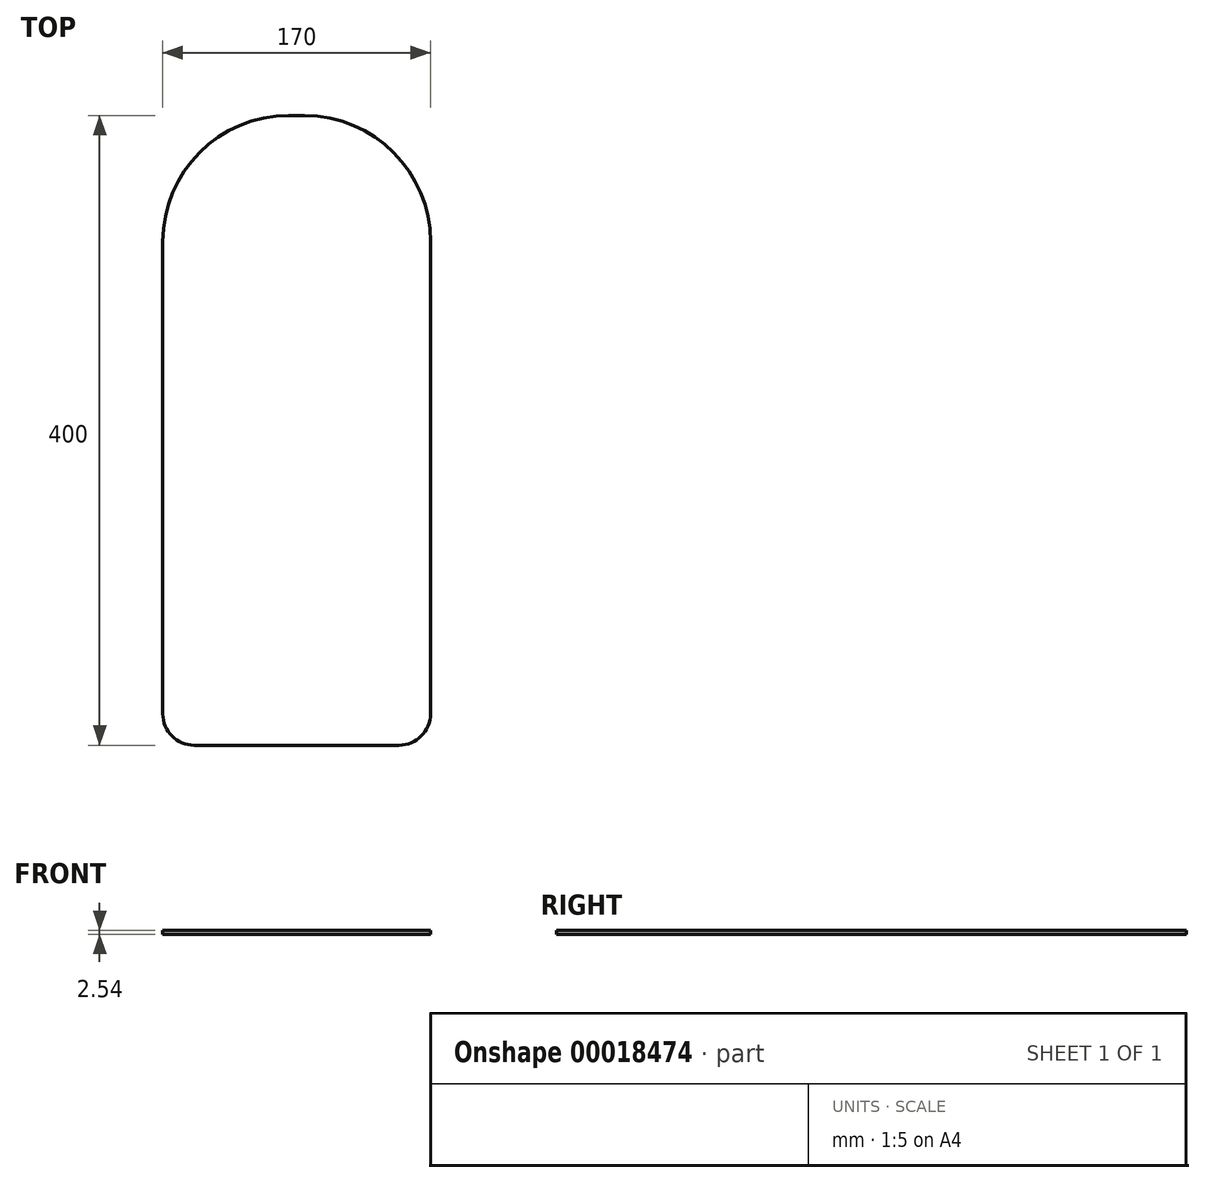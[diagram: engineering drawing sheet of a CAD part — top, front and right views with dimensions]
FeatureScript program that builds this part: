
annotation { "Feature Type Name" : "Feature", "Feature Type Description" : "" }
export const myFeature = defineFeature(function(context is Context, id is Id, definition is map)
    precondition{}
    {
        {
            var Q0;
            Q0=qCreatedBy(makeId("Top.planeOp"),FACE);
            var sketch = newSketch(context, id + "F0", { "sketchPlane" : qUnion([Q0])});
            skLineSegment(sketch, "E0.rect.bottom", {"start": v(65, -200) * mm, "end": v(-65, -200) * mm});
            skLineSegment(sketch, "E0.rect.top", {"start": v(5, 200) * mm, "end": v(-5, 200) * mm});
            skLineSegment(sketch, "E0.rect.left", {"start": v(85, -180) * mm, "end": v(85, 120) * mm});
            skLineSegment(sketch, "E0.rect.right", {"start": v(-85, -180) * mm, "end": v(-85, 120) * mm});
            skPoint(sketch, "E0.rect.middle", {"position": v(0, 0) * mm});
            skPoint(sketch, "E1.visualSharp", {"position": v(85, -200) * mm});
            skArc(sketch, "E1.filletArc", {"start": v(65, -200) * mm, "mid": v(79.14, -194.14) * mm, "end": v(85, -180) * mm});
            skPoint(sketch, "E2.visualSharp", {"position": v(-85, -200) * mm});
            skArc(sketch, "E2.filletArc", {"start": v(-85, -180) * mm, "mid": v(-79.14, -194.14) * mm, "end": v(-65, -200) * mm});
            skPoint(sketch, "E3.visualSharp", {"position": v(-85, 200) * mm});
            skArc(sketch, "E3.filletArc", {"start": v(-5, 200) * mm, "mid": v(-61.57, 176.57) * mm, "end": v(-85, 120) * mm});
            skPoint(sketch, "E4.visualSharp", {"position": v(85, 200) * mm});
            skArc(sketch, "E4.filletArc", {"start": v(85, 120) * mm, "mid": v(61.57, 176.57) * mm, "end": v(5, 200) * mm});
            skSolve(sketch);
        }
        {
            var Q0;
            Q0 = qSketchRegion(id + "F0", true);
            extrude(context, id + "F1", {"entities" : qUnion([Q0]), "depth" : 2.54 * mm});
        }
    });
